annotation { "Feature Type Name" : "Feature", "Feature Type Description" : "" }
export const myFeature = defineFeature(function(context is Context, id is Id, definition is map)
    precondition{}
    {
        {
            var Q0;
            Q0=qCreatedBy(makeId("Right.planeOp"),FACE);
            var sketch = newSketch(context, id + "F0", { "sketchPlane" : qUnion([Q0])});
            skLineSegment(sketch, "E0", {"start": v(0, 0) * mm, "end": v(-381, 0) * mm});
            skLineSegment(sketch, "E1", {"start": v(0, 0) * mm, "end": v(381, 0) * mm});
            skLineSegment(sketch, "E2", {"start": v(0, 0) * mm, "end": v(0, 190.5) * mm});
            skLineSegment(sketch, "E3", {"start": v(-381, 0) * mm, "end": v(0, 190.5) * mm});
            skLineSegment(sketch, "E4", {"start": v(381, 0) * mm, "end": v(0, 190.5) * mm});
            skLineSegment(sketch, "E5", {"start": v(-381, 0) * mm, "end": v(-457.2, 0) * mm});
            skLineSegment(sketch, "E6", {"start": v(0, 190.5) * mm, "end": v(0, 228.6) * mm});
            skLineSegment(sketch, "E7", {"start": v(-457.2, 0) * mm, "end": v(0, 228.6) * mm});
            skLineSegment(sketch, "E8", {"start": v(381, 0) * mm, "end": v(457.2, 0) * mm});
            skLineSegment(sketch, "E9", {"start": v(0, 228.6) * mm, "end": v(457.2, 0) * mm});
            skLineSegment(sketch, "E10", {"start": v(-381, 0) * mm, "end": v(-381, -279.4) * mm});
            skLineSegment(sketch, "E11", {"start": v(381, 0) * mm, "end": v(381, -279.4) * mm});
            skLineSegment(sketch, "E12", {"start": v(-381, -279.4) * mm, "end": v(381, -279.4) * mm});
            skLineSegment(sketch, "E13", {"start": v(-381, -279.4) * mm, "end": v(-381, -330.2) * mm});
            skLineSegment(sketch, "E14", {"start": v(-381, -330.2) * mm, "end": v(381, -330.2) * mm});
            skLineSegment(sketch, "E15", {"start": v(381, -279.4) * mm, "end": v(381, -330.2) * mm});
            skLineSegment(sketch, "E16", {"start": v(-279.4, -279.4) * mm, "end": v(-279.4, -101.6) * mm});
            skLineSegment(sketch, "E17", {"start": v(-279.4, -101.6) * mm, "end": v(-203.2, -101.6) * mm});
            skLineSegment(sketch, "E18", {"start": v(-203.2, -101.6) * mm, "end": v(-203.2, -279.4) * mm});
            skLineSegment(sketch, "E19.0", {"start": v(-177.8, -76.2) * mm, "end": v(-177.8, -279.4) * mm});
            skLineSegment(sketch, "E19.1", {"start": v(-304.8, -76.2) * mm, "end": v(-177.8, -76.2) * mm});
            skLineSegment(sketch, "E19.2", {"start": v(-304.8, -279.4) * mm, "end": v(-304.8, -76.2) * mm});
            skLineSegment(sketch, "E20", {"start": v(381, 0) * mm, "end": v(762, -50.27) * mm});
            skLineSegment(sketch, "E21", {"start": v(762, -50.27) * mm, "end": v(762, -278.87) * mm});
            skLineSegment(sketch, "E22", {"start": v(381, -279.4) * mm, "end": v(762, -278.87) * mm});
            skLineSegment(sketch, "E23", {"start": v(762, -278.87) * mm, "end": v(762.07, -329.67) * mm});
            skLineSegment(sketch, "E24", {"start": v(381, -330.2) * mm, "end": v(762.07, -329.67) * mm});
            skLineSegment(sketch, "E25", {"start": v(381, -50.8) * mm, "end": v(762, -101.07) * mm});
            skLineSegment(sketch, "E26.bottom", {"start": v(533.4, -220.85) * mm, "end": v(635, -220.85) * mm});
            skLineSegment(sketch, "E26.top", {"start": v(533.4, -119.25) * mm, "end": v(635, -119.25) * mm});
            skLineSegment(sketch, "E26.left", {"start": v(533.4, -220.85) * mm, "end": v(533.4, -119.25) * mm});
            skLineSegment(sketch, "E26.right", {"start": v(635, -220.85) * mm, "end": v(635, -119.25) * mm});
            skLineSegment(sketch, "E27.0", {"start": v(515.62, -101.47) * mm, "end": v(652.78, -101.47) * mm});
            skLineSegment(sketch, "E27.1", {"start": v(515.62, -238.63) * mm, "end": v(515.62, -101.47) * mm});
            skLineSegment(sketch, "E27.2", {"start": v(515.62, -238.63) * mm, "end": v(652.78, -238.63) * mm});
            skLineSegment(sketch, "E27.3", {"start": v(652.78, -238.63) * mm, "end": v(652.78, -101.47) * mm});
            skLineSegment(sketch, "E28", {"start": v(-49.25, -76.2) * mm, "end": v(-49.25, -177.8) * mm});
            skLineSegment(sketch, "E29", {"start": v(-49.25, -76.2) * mm, "end": v(179.35, -76.2) * mm});
            skLineSegment(sketch, "E30", {"start": v(179.35, -76.2) * mm, "end": v(179.35, -177.8) * mm});
            skLineSegment(sketch, "E31", {"start": v(-49.25, -177.8) * mm, "end": v(179.35, -177.8) * mm});
            skLineSegment(sketch, "E32.0", {"start": v(-36.55, -88.9) * mm, "end": v(166.65, -88.9) * mm});
            skLineSegment(sketch, "E32.1", {"start": v(-36.55, -88.9) * mm, "end": v(-36.55, -165.1) * mm});
            skLineSegment(sketch, "E32.2", {"start": v(-36.55, -165.1) * mm, "end": v(166.65, -165.1) * mm});
            skLineSegment(sketch, "E32.3", {"start": v(166.65, -88.9) * mm, "end": v(166.65, -165.1) * mm});
            skText(sketch, "E33", { "text": "Kaden Hodge", "fontName": "OpenSans-Regular.ttf"});
            const initialGuessF0  = {"E33": [-0.5678, 0.35696, 1, 0, 0.32808]};
            skSetInitialGuess(sketch, initialGuessF0);
            skSolve(sketch);
        }
        {
            var Q0;
            Q0=makeQuery(id+"F0.imprint","IMPRINT",FACE,{"disambiguationData":[TD([[makeQuery(id+"F0.imprint","IMPRINT",EDGE,{"derivedFrom":sQuery(id+"F0.wireOp",EDGE,"E0")}),-1.0]])]});
            var Q1;
            Q1=makeQuery(id+"F0.imprint","IMPRINT",FACE,{"disambiguationData":[TD([[makeQuery(id+"F0.imprint","IMPRINT",EDGE,{"derivedFrom":sQuery(id+"F0.wireOp",EDGE,"E1")}),1.0]])]});
            var Q2;
            Q2=makeQuery(id+"F0.imprint","IMPRINT",FACE,{"disambiguationData":[TD([[makeQuery(id+"F0.imprint","IMPRINT",EDGE,{"derivedFrom":sQuery(id+"F0.wireOp",EDGE,"E0")}),1.0]])]});
            var Q3;
            {var subQ1=sQuery(id+"F0.wireOp",EDGE,"E22");Q3=makeQuery(id+"F0.imprint","IMPRINT",FACE,{"disambiguationData":[TD([[makeQuery(id+"F0.imprint","IMPRINT",EDGE,{"derivedFrom":subQ1}),1.0]])]});}
            extrude(context, id + "F1", {"entities" : qUnion([Q0, Q1, Q2, Q3]), "endBound" : BoundingType.SYMMETRIC, "depth" : 1016 * mm, "offsetDistance" : 25.4 * mm});
        }
        {
            var Q0;
            {var subQ0=sQuery(id+"F0.wireOp",EDGE,"E16");Q0=makeQuery(id+"F0.imprint","IMPRINT",FACE,{"disambiguationData":[TD([[makeQuery(id+"F0.imprint","IMPRINT",EDGE,{"derivedFrom":subQ0}),1.0]])]});}
            var Q1;
            Q1=makeQuery(id+"F0.imprint","IMPRINT",FACE,{"disambiguationData":[TD([[makeQuery(id+"F0.imprint","IMPRINT",EDGE,{"derivedFrom":sQuery(id+"F0.wireOp",EDGE,"E26.bottom")}),-1.0]])]});
            var Q2;
            Q2=makeQuery(id+"F0.imprint","IMPRINT",FACE,{"disambiguationData":[TD([[makeQuery(id+"F0.imprint","IMPRINT",EDGE,{"derivedFrom":sQuery(id+"F0.wireOp",EDGE,"E28")}),1.0]])]});
            extrude(context, id + "F2", {"entities" : qUnion([Q0, Q1, Q2]), "depth" : 508 * mm, "offsetDistance" : 25.4 * mm});
        }
        {
            var Q0;
            Q0=makeQuery(id+"F0.imprint","IMPRINT",FACE,{"disambiguationData":[TD([[makeQuery(id+"F0.imprint","IMPRINT",EDGE,{"derivedFrom":sQuery(id+"F0.wireOp",EDGE,"E3")}),1.0]])]});
            var Q1;
            Q1=makeQuery(id+"F0.imprint","IMPRINT",FACE,{"disambiguationData":[TD([[makeQuery(id+"F0.imprint","IMPRINT",EDGE,{"derivedFrom":sQuery(id+"F0.wireOp",EDGE,"E4")}),-1.0]])]});
            var Q2;
            {var subQ0=sQuery(id+"F0.wireOp",EDGE,"E20");Q2=makeQuery(id+"F0.imprint","IMPRINT",FACE,{"disambiguationData":[TD([[makeQuery(id+"F0.imprint","IMPRINT",EDGE,{"derivedFrom":subQ0}),-1.0]])]});}
            extrude(context, id + "F3", {"entities" : qUnion([Q0, Q1, Q2]), "depth" : 599.95 * mm, "offsetDistance" : 25.4 * mm, "hasSecondDirection" : true, "secondDirectionOppositeDirection" : true, "secondDirectionDepth" : 612.14 * mm});
        }
    });